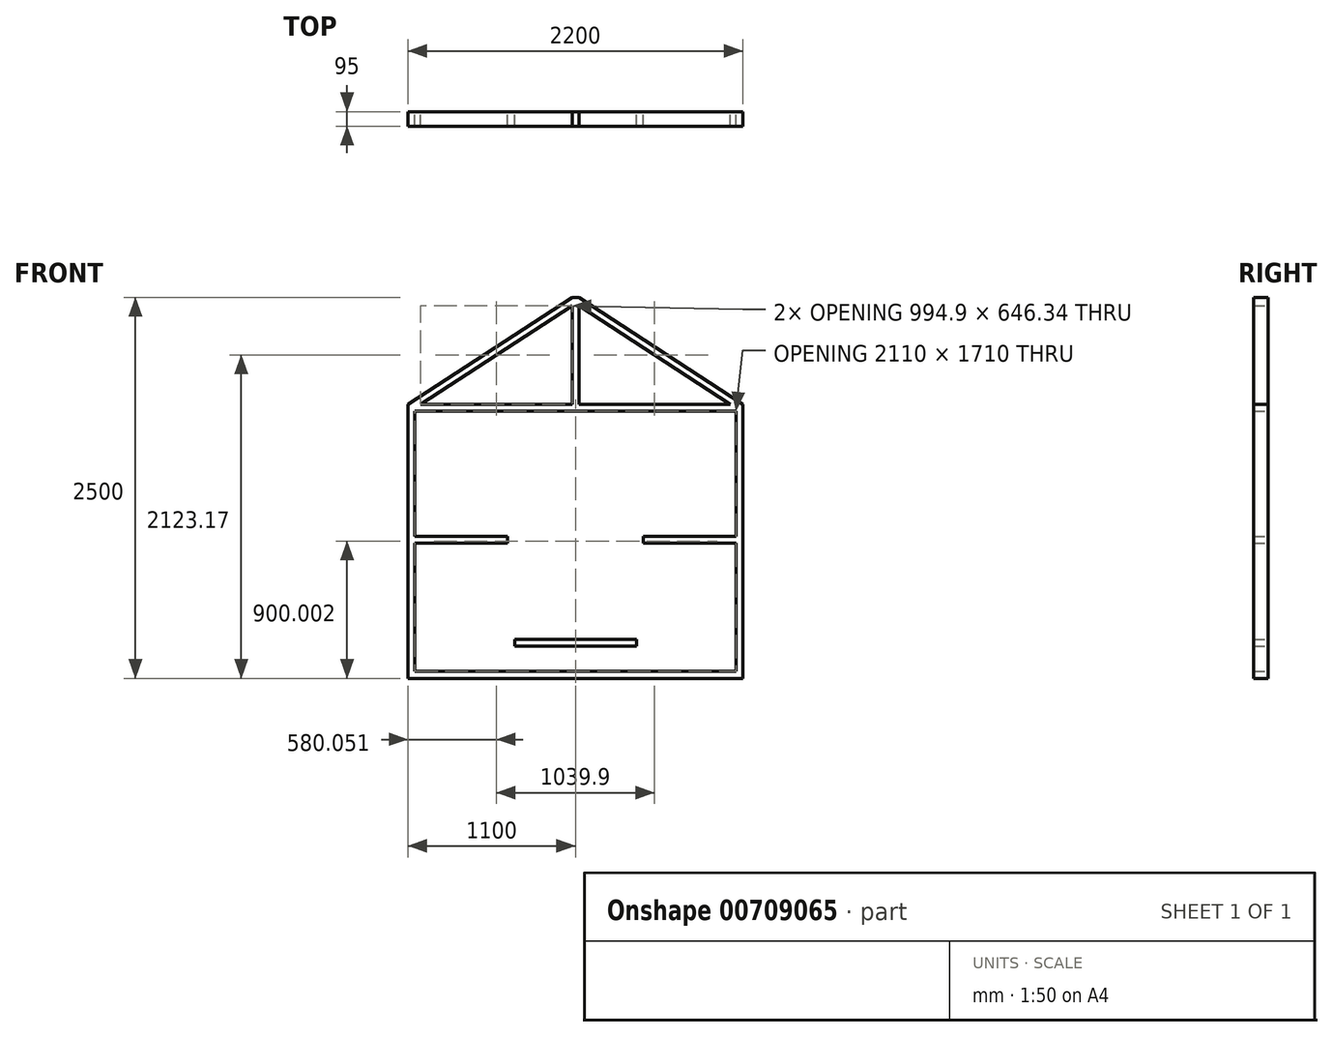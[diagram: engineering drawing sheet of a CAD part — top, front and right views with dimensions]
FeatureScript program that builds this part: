
annotation { "Feature Type Name" : "Feature", "Feature Type Description" : "" }
export const myFeature = defineFeature(function(context is Context, id is Id, definition is map)
    precondition{}
    {
        {
            var Q0;
            Q0=qCreatedBy(makeId("Front.planeOp"),FACE);
            var sketch = newSketch(context, id + "F0", { "sketchPlane" : qUnion([Q0])});
            skLineSegment(sketch, "E0.bottom", {"start": v(1100, -583.17) * mm, "end": v(-1100, -583.17) * mm});
            skLineSegment(sketch, "E0.top", {"start": v(1100, -628.17) * mm, "end": v(-1100, -628.17) * mm});
            skLineSegment(sketch, "E0.left", {"start": v(1100, -583.17) * mm, "end": v(1100, -628.17) * mm});
            skLineSegment(sketch, "E0.right", {"start": v(-1100, -583.17) * mm, "end": v(-1100, -628.17) * mm});
            skPoint(sketch, "E0.middle", {"position": v(0, -605.67) * mm});
            skLineSegment(sketch, "E1.bottom", {"start": v(1100, 1171.83) * mm, "end": v(-1100, 1171.83) * mm});
            skLineSegment(sketch, "E1.top", {"start": v(1100, 1126.83) * mm, "end": v(-1100, 1126.83) * mm});
            skLineSegment(sketch, "E1.left", {"start": v(1100, 1171.83) * mm, "end": v(1100, 1126.83) * mm});
            skLineSegment(sketch, "E1.right", {"start": v(-1100, 1171.83) * mm, "end": v(-1100, 1126.83) * mm});
            skPoint(sketch, "E1.middle", {"position": v(0, 1149.33) * mm});
            skLineSegment(sketch, "E2.bottom", {"start": v(1100, 1126.83) * mm, "end": v(1055, 1126.83) * mm});
            skLineSegment(sketch, "E2.top", {"start": v(1100, -583.17) * mm, "end": v(1055, -583.17) * mm});
            skLineSegment(sketch, "E2.left", {"start": v(1100, 1126.83) * mm, "end": v(1100, -583.17) * mm});
            skLineSegment(sketch, "E2.right", {"start": v(1055, 1126.83) * mm, "end": v(1055, -583.17) * mm});
            skLineSegment(sketch, "E3.bottom", {"start": v(-1100, 1126.83) * mm, "end": v(-1055, 1126.83) * mm});
            skLineSegment(sketch, "E3.top", {"start": v(-1100, -583.17) * mm, "end": v(-1055, -583.17) * mm});
            skLineSegment(sketch, "E3.left", {"start": v(-1100, 1126.83) * mm, "end": v(-1100, -583.17) * mm});
            skLineSegment(sketch, "E3.right", {"start": v(-1055, 1126.83) * mm, "end": v(-1055, -583.17) * mm});
            skLineSegment(sketch, "E4.bottom", {"start": v(-445, -583.17) * mm, "end": v(-400, -583.17) * mm});
            skLineSegment(sketch, "E4.top", {"start": v(-445, 1126.83) * mm, "end": v(-400, 1126.83) * mm});
            skLineSegment(sketch, "E4.left", {"start": v(-445, -583.17) * mm, "end": v(-445, 1126.83) * mm});
            skLineSegment(sketch, "E4.right", {"start": v(-400, -583.17) * mm, "end": v(-400, 1126.83) * mm});
            skLineSegment(sketch, "E5.bottom", {"start": v(400, 1126.83) * mm, "end": v(445, 1126.83) * mm});
            skLineSegment(sketch, "E5.top", {"start": v(400, -583.17) * mm, "end": v(445, -583.17) * mm});
            skLineSegment(sketch, "E5.left", {"start": v(445, 1126.83) * mm, "end": v(445, -583.17) * mm});
            skLineSegment(sketch, "E5.right", {"start": v(400, 1126.83) * mm, "end": v(400, -583.17) * mm});
            skLineSegment(sketch, "E6.bottom", {"start": v(-400, -373.17) * mm, "end": v(400, -373.17) * mm});
            skLineSegment(sketch, "E6.top", {"start": v(-400, -418.17) * mm, "end": v(400, -418.17) * mm});
            skLineSegment(sketch, "E6.left", {"start": v(-400, -373.17) * mm, "end": v(-400, -418.17) * mm});
            skLineSegment(sketch, "E6.right", {"start": v(400, -373.17) * mm, "end": v(400, -418.17) * mm});
            skLineSegment(sketch, "E7", {"start": v(-1055, 259.83) * mm, "end": v(-445, 259.83) * mm});
            skLineSegment(sketch, "E8", {"start": v(-1055, 304.83) * mm, "end": v(-445, 304.83) * mm});
            skLineSegment(sketch, "E9.MirrorCS", {"start": v(1055, 259.83) * mm, "end": v(445, 259.83) * mm});
            skLineSegment(sketch, "E10.MirrorCS", {"start": v(1055, 304.83) * mm, "end": v(445, 304.83) * mm});
            skLineSegment(sketch, "E11.bottom", {"start": v(-22.5, 1171.83) * mm, "end": v(22.5, 1171.83) * mm});
            skLineSegment(sketch, "E11.top", {"start": v(-22.5, 1871.83) * mm, "end": v(22.5, 1871.83) * mm});
            skLineSegment(sketch, "E11.left", {"start": v(-22.5, 1171.83) * mm, "end": v(-22.5, 1871.83) * mm});
            skLineSegment(sketch, "E11.right", {"start": v(22.5, 1171.83) * mm, "end": v(22.5, 1871.83) * mm});
            skLineSegment(sketch, "E12", {"start": v(-1100, 1171.83) * mm, "end": v(-22.5, 1871.83) * mm});
            skLineSegment(sketch, "E13", {"start": v(22.5, 1871.83) * mm, "end": v(1100, 1171.83) * mm});
            skLineSegment(sketch, "E14", {"start": v(-1017.4, 1171.83) * mm, "end": v(-22.5, 1818.17) * mm});
            skLineSegment(sketch, "E15", {"start": v(22.5, 1818.17) * mm, "end": v(1017.4, 1171.83) * mm});
            skSolve(sketch);
        }
        {
            var Q0;
            Q0 = qSketchRegion(id + "F0", true);
            var Q1;
            {var subQ0=sQuery(id+"F0.wireOp",EDGE,"apKnzXqb-7Lmc-cgBK-WmSE-JRUgLc3Nn7XE");Q1=makeQuery(id+"F0.imprint","IMPRINT",FACE,{"disambiguationData":[TD([[makeQuery(id+"F0.imprint","IMPRINT",EDGE,{"derivedFrom":subQ0}),1.0]])]});}
            var Q2;
            {var subQ3=sQuery(id+"F0.wireOp",EDGE,"E4.bottom");Q2=makeQuery(id+"F0.imprint","IMPRINT",FACE,{"disambiguationData":[TD([[makeQuery(id+"F0.imprint","IMPRINT",EDGE,{"derivedFrom":subQ3}),1.0]])]});}
            var Q3;
            {var subQ3=sQuery(id+"F0.wireOp",EDGE,"E5.bottom");Q3=makeQuery(id+"F0.imprint","IMPRINT",FACE,{"disambiguationData":[TD([[makeQuery(id+"F0.imprint","IMPRINT",EDGE,{"derivedFrom":subQ3}),-1.0]])]});}
            var Q4;
            {var subQ0=sQuery(id+"F0.wireOp",EDGE,"E9.MirrorCS");Q4=makeQuery(id+"F0.imprint","IMPRINT",FACE,{"disambiguationData":[TD([[makeQuery(id+"F0.imprint","IMPRINT",EDGE,{"derivedFrom":subQ0}),-1.0]])]});}
            var Q5;
            {var subQ0=sQuery(id+"F0.wireOp",EDGE,"E7");Q5=makeQuery(id+"F0.imprint","IMPRINT",FACE,{"disambiguationData":[TD([[makeQuery(id+"F0.imprint","IMPRINT",EDGE,{"derivedFrom":subQ0}),1.0]])]});}
            var Q6;
            Q6=makeQuery(id+"F0.imprint","IMPRINT",FACE,{"disambiguationData":[TD([[makeQuery(id+"F0.imprint","IMPRINT",EDGE,{"derivedFrom":sQuery(id+"F0.wireOp",EDGE,"E6.bottom")}),-1.0]])]});
            extrude(context, id + "F1", {"entities" : qUnion([Q0, Q1, Q2, Q3, Q4, Q5, Q6]), "depth" : 95 * mm, "offsetDistance" : 25 * mm});
        }
    });
